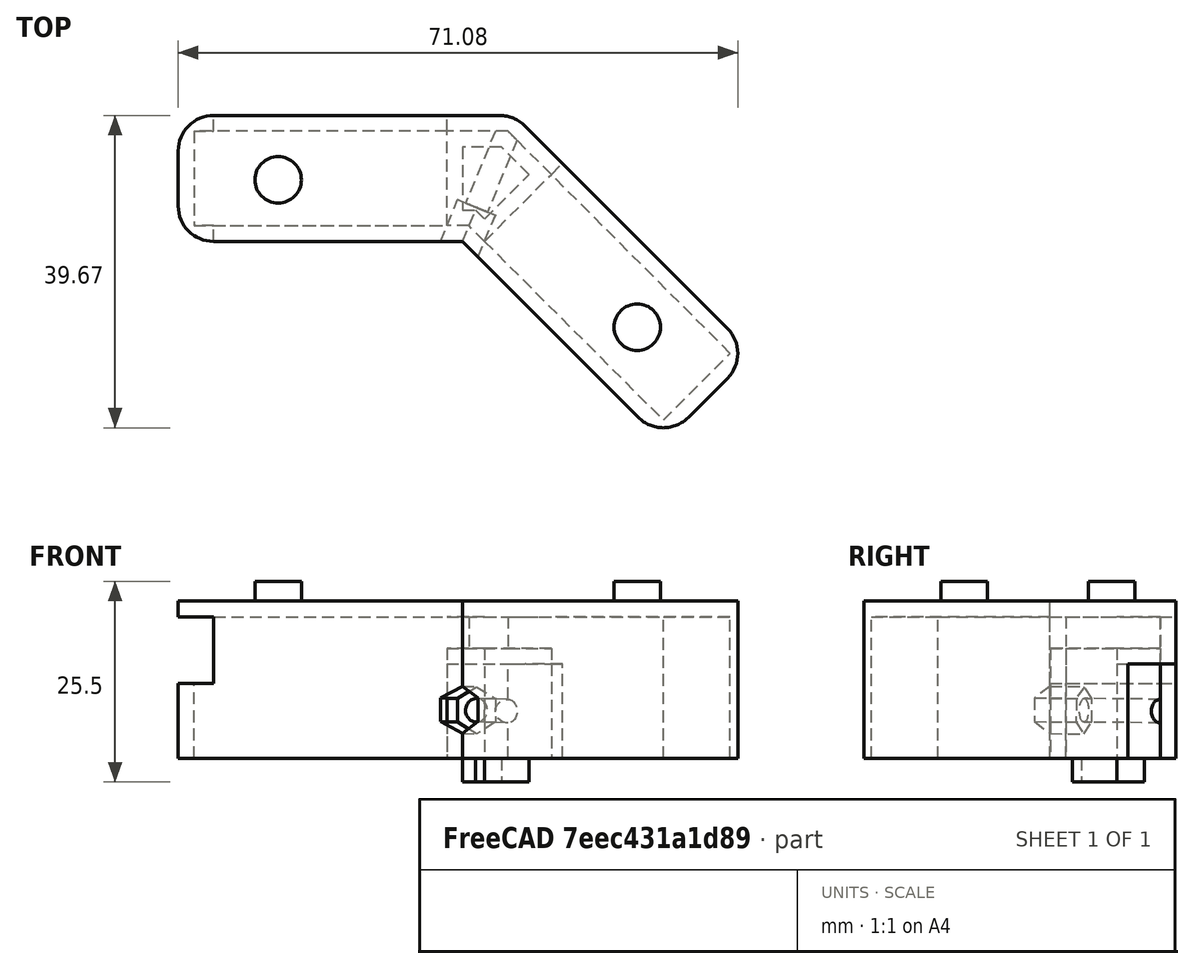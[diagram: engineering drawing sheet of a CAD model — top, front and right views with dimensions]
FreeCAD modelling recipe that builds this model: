
FCSTD DOCUMENT  (FreeCAD 0.19R)
Label: femur_btm
License: All rights reserved
LicenseURL: http://en.wikipedia.org/wiki/All_rights_reserved
objects: Sketcher::SketchObject×10, PartDesign::Pocket×6, PartDesign::Pad×4, PartDesign::Plane×1, PartDesign::Body×1
note: 32 computed .brp shape members not serialized (recipe doc carries the construction recipe); baked Part::Feature solids carry a one-line shape summary decoded from their .brp

FEATURE [Sketcher::SketchObject] Sketch004
  MapMode = 5
  Support = -> [XY_Plane001]
  sketch-geometry (21):
    g0: LineSegment [constr] StartX=-10.9452 StartY=6.06643 StartZ=0 EndX=20.9548 EndY=6.06643 EndZ=0
    g1: LineSegment [constr] StartX=20.9548 StartY=6.06643 StartZ=0 EndX=20.9548 EndY=-5.73357 EndZ=0
    g2: LineSegment [constr] StartX=20.9548 StartY=-5.73357 StartZ=0 EndX=-10.9452 EndY=-5.73357 EndZ=0
    g3: LineSegment [constr] StartX=-10.9452 StartY=-5.73357 StartZ=0 EndX=-10.9452 EndY=6.06643 EndZ=0
    g4: LineSegment StartX=-13.0452 StartY=-3.33357 StartZ=0 EndX=-13.0452 EndY=3.66643 EndZ=0
    g5: LineSegment StartX=-8.54522 StartY=8.16643 StartZ=0 EndX=27.8182 EndY=8.16643 EndZ=0
    g6: LineSegment StartX=31.0002 StartY=6.84841 StartZ=0 EndX=56.7131 EndY=-18.8644 EndZ=0
    g7: LineSegment StartX=56.7131 StartY=-25.2284 StartZ=0 EndX=51.7633 EndY=-30.1781 EndZ=0
    g8: LineSegment StartX=45.3994 StartY=-30.1781 StartZ=0 EndX=23.0548 EndY=-7.83357 EndZ=0
    g9: LineSegment StartX=23.0548 StartY=-7.83357 StartZ=0 EndX=-8.54522 EndY=-7.83357 EndZ=0
    g10: LineSegment [constr] StartX=-13.0452 StartY=3.66643 StartZ=0 EndX=-10.9452 EndY=3.66643 EndZ=0
    g11: LineSegment [constr] StartX=-8.54522 StartY=8.16643 StartZ=0 EndX=-8.54522 EndY=6.06643 EndZ=0
    g12: LineSegment [constr] StartX=-8.54522 StartY=-5.73357 StartZ=0 EndX=-8.54522 EndY=-7.83357 EndZ=0
    g13: LineSegment [constr] StartX=23.0548 StartY=-7.83357 StartZ=0 EndX=23.0548 EndY=8.16643 EndZ=0
    g14: LineSegment [constr] StartX=20.9548 StartY=-5.73357 StartZ=0 EndX=23.0548 EndY=-5.73357 EndZ=0
    g15: ArcOfCircle CenterX=-8.54522 CenterY=-3.33357 CenterZ=0 NormalX=0 NormalY=0 NormalZ=1 AngleXU=0 Radius=4.5 StartAngle=3.14159 EndAngle=4.71239
    g16: ArcOfCircle CenterX=-8.54522 CenterY=3.66643 CenterZ=0 NormalX=0 NormalY=0 NormalZ=1 AngleXU=0 Radius=4.5 StartAngle=1.5708 EndAngle=3.14159
    g17: ArcOfCircle CenterX=27.8182 CenterY=3.66643 CenterZ=0 NormalX=0 NormalY=0 NormalZ=1 AngleXU=0 Radius=4.5 StartAngle=0.785398 EndAngle=1.5708
    g18: ArcOfCircle CenterX=53.5311 CenterY=-22.0464 CenterZ=0 NormalX=0 NormalY=0 NormalZ=1 AngleXU=0 Radius=4.5 StartAngle=5.49779 EndAngle=7.06858
    g19: ArcOfCircle CenterX=48.5813 CenterY=-26.9962 CenterZ=0 NormalX=0 NormalY=0 NormalZ=1 AngleXU=0 Radius=4.5 StartAngle=3.92699 EndAngle=5.49779
    g20: LineSegment [constr] StartX=23.0548 StartY=-7.83357 StartZ=0 EndX=34.3685 EndY=3.48014 EndZ=0
  constraints (56):
    c: Coincident(g0,g1)
    c: Coincident(g1,g2)
    c: Coincident(g2,g3)
    c: Coincident(g3,g0)
    c: Horizontal(g0)
    c: Horizontal(g2)
    c: Vertical(g1)
    c: Vertical(g3)
    c: DistanceX(g0,g0) = 31.9
    c: DistanceY(g1,g1) = 11.8
    c: Vertical(g4)
    c: Horizontal(g5)
    c: Coincident(g8,g9)
    c: Horizontal(g9)
    c: Angle(g9,g8) = 2.35619
    c: Parallel(g8,g6)
    c: Perpendicular(g7,g8)
    c: Horizontal(g10)
    c: Vertical(g11)
    c: Vertical(g12)
    c: PointOnObject(g10,g3)
    c: PointOnObject(g11,g0)
    c: PointOnObject(g12,g2)
    c: Equal(g11,g10)
    c: Equal(g10,g12)
    c: DistanceY(g12,g12) = 2.1
    c: Coincident(g13,g8)
    c: PointOnObject(g13,g5)
    c: Vertical(g13)
    c: PointOnObject(g14,g13)
    c: Horizontal(g14)
    c: Equal(g14,g12)
    c: Tangent(g4,g15) = 1.5708
    c: Tangent(g9,g15) = 1.5708
    c: Tangent(g4,g16) = 1.5708
    c: Tangent(g5,g16) = 1.5708
    c: Tangent(g5,g17) = 1.5708
    c: Tangent(g6,g17) = 1.5708
    c: Tangent(g6,g18) = 1.5708
    c: Tangent(g7,g18) = 1.5708
    c: Tangent(g7,g19) = 1.5708
    c: Tangent(g8,g19) = 1.5708
    c: Equal(g19,g18)
    c: Equal(g18,g17)
    c: Equal(g17,g16)
    c: Equal(g16,g15)
    c: Radius(g18) = 4.5
    c: Equal(g8,g9)
    c: Coincident(g20,g8)
    c: PointOnObject(g20,g6)
    c: Perpendicular(g20,g8)
    c: Coincident(g10,g4)
    c: Coincident(g11,g5)
    c: Coincident(g12,g9)
    c: Coincident(g14,g1)
    c: Equal(g20,g13)
FEATURE [PartDesign::Pad] Pad003
  Length = 20
  Length2 = 100
  Profile = -> Sketch004
  Type = 0
FEATURE [Sketcher::SketchObject] Sketch005
  ExternalGeometry = -> [Pad003]
  MapMode = 5
  Placement = pos=(0,0,0) rot=(1,0,0;3.14159rad)
  Support = -> [Pad003]
  sketch-geometry (10):
    g0: LineSegment StartX=-11.0452 StartY=-6.16643 StartZ=0 EndX=-11.0452 EndY=5.83357 EndZ=0
    g1: LineSegment StartX=-11.0452 StartY=5.83357 StartZ=0 EndX=23.8832 EndY=5.83357 EndZ=0
    g2: LineSegment StartX=23.8832 StartY=5.83357 StartZ=0 EndX=48.5813 EndY=30.5317 EndZ=0
    g3: LineSegment StartX=48.5813 StartY=30.5317 StartZ=0 EndX=57.0666 EndY=22.0464 EndZ=0
    g4: LineSegment StartX=57.0666 StartY=22.0464 StartZ=0 EndX=28.8538 EndY=-6.16643 EndZ=0
    g5: LineSegment StartX=28.8538 StartY=-6.16643 StartZ=0 EndX=-11.0452 EndY=-6.16643 EndZ=0
    g6: LineSegment [constr] StartX=-13.0452 StartY=-3.66643 StartZ=0 EndX=-11.0452 EndY=-3.66643 EndZ=0
    g7: LineSegment [constr] StartX=-8.54522 StartY=7.83357 StartZ=0 EndX=-8.54522 EndY=5.83357 EndZ=0
    g8: LineSegment [constr] StartX=-8.54522 StartY=-8.16643 StartZ=0 EndX=-8.54522 EndY=-6.16643 EndZ=0
    g9: LineSegment [constr] StartX=51.7633 StartY=30.1781 StartZ=0 EndX=50.3491 EndY=28.7639 EndZ=0
  constraints (30):
    c: Vertical(g0)
    c: Coincident(g0,g1)
    c: Horizontal(g1)
    c: Coincident(g1,g2)
    c: Coincident(g2,g3)
    c: Coincident(g3,g4)
    c: Coincident(g4,g5)
    c: Coincident(g5,g0)
    c: Horizontal(g5)
    c: Coincident(g6,g-3)
    c: PointOnObject(g6,g0)
    c: Horizontal(g6)
    c: Coincident(g7,g-4)
    c: PointOnObject(g7,g1)
    c: Vertical(g7)
    c: Coincident(g8,g-5)
    c: PointOnObject(g8,g5)
    c: Vertical(g8)
    c: Equal(g8,g6)
    c: Equal(g6,g7)
    c: DistanceY(g8,g8) = 2
    c: Equal(g0,g3)
    c: Perpendicular(g3,g4)
    c: Parallel(g2,g4)
    c: Parallel(g4,g-6)
    c: Equal(g4,g5)
    c: Coincident(g9,g-7)
    c: PointOnObject(g9,g3)
    c: Perpendicular(g3,g9)
    c: Equal(g9,g8)
FEATURE [PartDesign::Pocket] Pocket001
  BaseFeature = -> Pad003
  Length = 18
  Length2 = 100
  Profile = -> Sketch005
  Type = 0
FEATURE [Sketcher::SketchObject] Sketch
  ExternalGeometry = -> [Pocket001]
  MapMode = 5
  Placement = pos=(0,-7.83357,0) rot=(1,0,0;1.5708rad)
  Support = -> [Pocket001]
  sketch-geometry (5):
    g0: GeomPoint X=-8.54522 Y=18 Z=0
    g1: LineSegment StartX=-8.54522 StartY=18 StartZ=0 EndX=-13.0452 EndY=18 EndZ=0
    g2: LineSegment StartX=-13.0452 StartY=18 StartZ=0 EndX=-13.0452 EndY=9.5 EndZ=0
    g3: LineSegment StartX=-13.0452 StartY=9.5 StartZ=0 EndX=-8.54522 EndY=9.5 EndZ=0
    g4: LineSegment StartX=-8.54522 StartY=9.5 StartZ=0 EndX=-8.54522 EndY=18 EndZ=0
  constraints (13):
    c: PointOnObject(g0,g-4)
    c: PointOnObject(g0,g-3)
    c: Coincident(g1,g2)
    c: Coincident(g2,g3)
    c: Coincident(g3,g4)
    c: Coincident(g4,g1)
    c: Horizontal(g1)
    c: Horizontal(g3)
    c: Vertical(g2)
    c: Vertical(g4)
    c: Coincident(g1,g0)
    c: PointOnObject(g2,g-5)
    c: DistanceY(g2,g2) = 8.5
FEATURE [PartDesign::Pocket] Pocket
  BaseFeature = -> Pocket001
  Length = 5
  Length2 = 100
  Profile = -> Sketch
  Type = 1
FEATURE [Sketcher::SketchObject] Sketch006
  ExternalGeometry = -> [Pocket]
  MapMode = 5
  Placement = pos=(0,0,18) rot=(1,0,0;3.14159rad)
  Support = -> [Pocket]
  sketch-geometry (6):
    g0: LineSegment StartX=21.0832 StartY=5.83357 StartZ=0 EndX=21.0832 EndY=-6.16643 EndZ=0
    g1: LineSegment StartX=25.8631 StartY=7.81346 StartZ=0 EndX=34.3484 EndY=-0.671817 EndZ=0
    g2: LineSegment StartX=21.0832 StartY=5.83357 StartZ=0 EndX=23.8832 EndY=5.83357 EndZ=0
    g3: LineSegment StartX=23.8832 StartY=5.83357 StartZ=0 EndX=25.8631 EndY=7.81346 EndZ=0
    g4: LineSegment StartX=34.3484 StartY=-0.671817 StartZ=0 EndX=28.8538 EndY=-6.16643 EndZ=0
    g5: LineSegment StartX=28.8538 StartY=-6.16643 StartZ=0 EndX=21.0832 EndY=-6.16643 EndZ=0
  constraints (16):
    c: Vertical(g0)
    c: Perpendicular(g1,g-5)
    c: PointOnObject(g1,g-5)
    c: PointOnObject(g0,g-6)
    c: PointOnObject(g0,g-3)
    c: PointOnObject(g1,g-4)
    c: Coincident(g0,g2)
    c: Coincident(g2,g-6)
    c: Coincident(g2,g3)
    c: Coincident(g3,g1)
    c: Coincident(g0,g5)
    c: Coincident(g5,g-4)
    c: Coincident(g4,g5)
    c: Coincident(g1,g4)
    c: Distance(g3) = 2.8
    c: Equal(g2,g3)
FEATURE [PartDesign::Pad] Pad
  BaseFeature = -> Pocket
  Length = 10
  Length2 = 100
  Profile = -> Sketch006
  Type = 3
  UpToFace = -> Pocket [Face4]
FEATURE [Sketcher::SketchObject] Sketch007
  ExternalGeometry = -> [Pad]
  MapMode = 5
  Placement = pos=(0,0,0) rot=(1,0,0;3.14159rad)
  Support = -> [Pad]
  sketch-geometry (7):
    g0: LineSegment [constr] StartX=23.8832 StartY=5.83357 StartZ=0 EndX=28.8538 EndY=-6.16643 EndZ=0
    g1: LineSegment StartX=23.0832 StartY=3.83357 StartZ=0 EndX=24.7116 EndY=3.83357 EndZ=0
    g2: LineSegment StartX=24.7116 StartY=3.83357 StartZ=0 EndX=25.8631 EndY=4.98504 EndZ=0
    g3: LineSegment StartX=25.8631 StartY=4.98504 StartZ=0 EndX=31.52 EndY=-0.671817 EndZ=0
    g4: LineSegment StartX=31.52 StartY=-0.671817 StartZ=0 EndX=28.0253 EndY=-4.16643 EndZ=0
    g5: LineSegment StartX=28.0253 StartY=-4.16643 StartZ=0 EndX=23.0832 EndY=-4.16643 EndZ=0
    g6: LineSegment StartX=23.0832 StartY=-4.16643 StartZ=0 EndX=23.0832 EndY=3.83357 EndZ=0
  constraints (20):
    c: Coincident(g0,g-3)
    c: Coincident(g0,g-4)
    c: PointOnObject(g1,g0)
    c: Coincident(g1,g2)
    c: Coincident(g2,g3)
    c: Coincident(g3,g4)
    c: PointOnObject(g4,g0)
    c: Coincident(g4,g5)
    c: Horizontal(g5)
    c: Coincident(g5,g6)
    c: Coincident(g6,g1)
    c: Vertical(g6)
    c: Horizontal(g1)
    c: Parallel(g-5,g2)
    c: Parallel(g2,g4)
    c: Equal(g1,g2)
    c: Equal(g5,g4)
    c: Distance(g1,g-3) = 2
    c: Distance(g3,g-4) = 2
    c: Distance(g5,g-6) = 2
FEATURE [PartDesign::Pad] Pad004
  BaseFeature = -> Pad
  Length = 3
  Length2 = 100
  Profile = -> Sketch007
  Type = 0
FEATURE [Sketcher::SketchObject] Sketch008
  ExternalGeometry = -> [Pad004]
  MapMode = 5
  Placement = pos=(0,0,0) rot=(1,0,0;3.14159rad)
  Support = -> [Pad004]
  sketch-geometry (7):
    g0: LineSegment StartX=21.0832 StartY=-6.16643 StartZ=0 EndX=21.0832 EndY=-8.16643 EndZ=0
    g1: LineSegment StartX=34.3484 StartY=-0.671817 StartZ=0 EndX=35.7626 EndY=-2.08603 EndZ=0
    g2: LineSegment StartX=21.0832 StartY=-8.16643 StartZ=0 EndX=27.8182 EndY=-8.16643 EndZ=0
    g3: LineSegment StartX=35.7626 StartY=-2.08603 StartZ=0 EndX=31.0002 EndY=-6.84841 EndZ=0
    g4: ArcOfCircle CenterX=27.8182 CenterY=-3.66643 CenterZ=0 NormalX=0 NormalY=0 NormalZ=1 AngleXU=0 Radius=4.5 StartAngle=4.71239 EndAngle=5.49779
    g5: LineSegment StartX=21.0832 StartY=-6.16643 StartZ=0 EndX=28.8538 EndY=-6.16643 EndZ=0
    g6: LineSegment StartX=28.8538 StartY=-6.16643 StartZ=0 EndX=34.3484 EndY=-0.671817 EndZ=0
  constraints (15):
    c: Coincident(g0,g-3)
    c: PointOnObject(g0,g-6)
    c: Vertical(g0)
    c: Coincident(g1,g-4)
    c: Perpendicular(g1,g-5)
    c: Coincident(g2,g0)
    c: Coincident(g3,g1)
    c: Tangent(g2,g4) = -1.5708
    c: Tangent(g3,g4) = 1.5708
    c: Coincident(g3,g-5)
    c: Coincident(g2,g-6)
    c: Coincident(g0,g5)
    c: Coincident(g5,g-7)
    c: Coincident(g5,g6)
    c: Coincident(g6,g1)
FEATURE [PartDesign::Pocket] Pocket002
  BaseFeature = -> Pad004
  Length = 12
  Length2 = 100
  Profile = -> Sketch008
  Type = 0
FEATURE [PartDesign::Plane] DatumPlane
  AttachmentOffset = pos=(-6,0,0) rot=(0,1,0;1.5708rad)
  Length = 64.9992
  MapMode = 45
  Placement = pos=(20.9961,-12.8037,1.05295) rot=(-0.48682,0.728578,0.481851;1.89204rad)
  ResizeMode = 0
  Support = -> [Sketch004,Pocket002]
  Width = 112.435
FEATURE [Sketcher::SketchObject] Sketch009
  ExternalGeometry = -> [Pocket002]
  MapMode = 5
  Placement = pos=(20.9961,-12.8037,1.05295) rot=(-0.48682,0.728578,0.481851;1.89204rad)
  Support = -> [DatumPlane]
  sketch-geometry (3):
    g0: Circle CenterX=-5.15743 CenterY=-4.5919e-12 CenterZ=0 NormalX=0 NormalY=0 NormalZ=1 AngleXU=0 Radius=1.5
    g1: LineSegment [constr] StartX=-11.1571 StartY=-4.4906e-12 StartZ=0 EndX=-5.15743 EndY=-4.5919e-12 EndZ=0
    g2: LineSegment [constr] StartX=-5.15743 StartY=-4.5919e-12 StartZ=0 EndX=0.842251 EndY=-4.6931e-12 EndZ=0
  constraints (7):
    c: Radius(g0) = 1.5
    c: Coincident(g1,g2)
    c: Coincident(g2,g-3)
    c: Coincident(g1,g-3)
    c: PointOnObject(g1,g-3)
    c: Equal(g1,g2)
    c: Coincident(g0,g1)
FEATURE [PartDesign::Pocket] Pocket003
  BaseFeature = -> Pocket002
  Length = 5
  Length2 = 100
  Profile = -> Sketch009
  Reversed = true
  Type = 1
FEATURE [Sketcher::SketchObject] Sketch010
  ExternalGeometry = -> [Pocket003,Pocket002]
  MapMode = 5
  Placement = pos=(20.9961,-12.8037,1.05295) rot=(-0.48682,0.728578,0.481851;1.89204rad)
  Support = -> [DatumPlane]
  sketch-geometry (9):
    g0: LineSegment [constr] StartX=-11.1571 StartY=-4.4906e-12 StartZ=0 EndX=-5.15743 EndY=-4.5919e-12 EndZ=0
    g1: LineSegment [constr] StartX=-5.15743 StartY=-4.5919e-12 StartZ=0 EndX=0.842251 EndY=-4.6931e-12 EndZ=0
    g2: LineSegment StartX=-3.65743 StartY=-2.59808 StartZ=0 EndX=-2.15743 EndY=-4.6425e-12 EndZ=0
    g3: LineSegment StartX=-2.15743 StartY=-4.6425e-12 StartZ=0 EndX=-3.65743 EndY=2.59808 EndZ=0
    g4: LineSegment StartX=-3.65743 StartY=2.59808 StartZ=0 EndX=-6.65743 EndY=2.59808 EndZ=0
    g5: LineSegment StartX=-6.65743 StartY=2.59808 StartZ=0 EndX=-8.15743 EndY=-4.5408e-12 EndZ=0
    g6: LineSegment StartX=-8.15743 StartY=-4.541e-12 StartZ=0 EndX=-6.65743 EndY=-2.59808 EndZ=0
    g7: LineSegment StartX=-6.65743 StartY=-2.59808 StartZ=0 EndX=-3.65743 EndY=-2.59808 EndZ=0
    g8: Circle [constr] CenterX=-5.15743 CenterY=-4.5919e-12 CenterZ=0 NormalX=0 NormalY=0 NormalZ=1 AngleXU=0 Radius=3
  constraints (21):
    c: Coincident(g0,g1)
    c: Coincident(g1,g-4)
    c: Coincident(g0,g-4)
    c: PointOnObject(g0,g-4)
    c: Equal(g0,g1)
    c: Coincident(g2,g3)
    c: Coincident(g3,g4)
    c: Coincident(g4,g5)
    c: Coincident(g5,g6)
    c: Coincident(g6,g7)
    c: Coincident(g7,g2)
    c: Equal(g2, g3-g7) x5
    c: PointOnObject(g2,g8)
    c: PointOnObject(g3,g8)
    c: PointOnObject(g4,g8)
    c: PointOnObject(g5,g8)
    c: PointOnObject(g6,g8)
    c: PointOnObject(g7,g8)
    c: Coincident(g8,g0)
    c: PointOnObject(g2,g0)
    c: Radius(g8) = 3
FEATURE [PartDesign::Pocket] Pocket004
  BaseFeature = -> Pocket003
  Length = 10
  Length2 = 100
  Profile = -> Sketch010
  Reversed = true
  Type = 0
FEATURE [Sketcher::SketchObject] Sketch011
  ExternalGeometry = -> [Pocket004]
  MapMode = 5
  Placement = pos=(0,0,18) rot=(1,0,0;3.14159rad)
  Support = -> [Pocket004]
  sketch-geometry (6):
    g0: LineSegment StartX=21.0832 StartY=5.83357 StartZ=0 EndX=21.0832 EndY=-6.16643 EndZ=0
    g1: LineSegment StartX=21.0832 StartY=-6.16643 StartZ=0 EndX=28.8538 EndY=-6.16643 EndZ=0
    g2: LineSegment StartX=28.8538 StartY=-6.16643 StartZ=0 EndX=34.3484 EndY=-0.671817 EndZ=0
    g3: LineSegment StartX=34.3484 StartY=-0.671817 StartZ=0 EndX=25.8631 EndY=7.81346 EndZ=0
    g4: LineSegment StartX=25.8631 StartY=7.81346 StartZ=0 EndX=23.8832 EndY=5.83357 EndZ=0
    g5: LineSegment StartX=23.8832 StartY=5.83357 StartZ=0 EndX=21.0832 EndY=5.83357 EndZ=0
  constraints (12):
    c: Coincident(g-5,g0)
    c: Coincident(g0,g-7)
    c: Coincident(g0,g1)
    c: Coincident(g1,g-8)
    c: Coincident(g1,g2)
    c: Coincident(g2,g-8)
    c: Coincident(g2,g3)
    c: Coincident(g3,g-6)
    c: Coincident(g3,g4)
    c: Coincident(g4,g-6)
    c: Coincident(g4,g5)
    c: Coincident(g5,g0)
FEATURE [PartDesign::Pocket] Pocket005
  BaseFeature = -> Pocket004
  Length = 4
  Length2 = 100
  Profile = -> Sketch011
  Reversed = true
  Type = 0
FEATURE [Sketcher::SketchObject] Sketch012
  ExternalGeometry = -> [Pocket005]
  MapMode = 5
  Placement = pos=(0,0,20) rot=(0,0,1;0rad)
  Support = -> [Pocket005]
  sketch-geometry (5):
    g0: LineSegment [constr] StartX=-13.0452 StartY=0 StartZ=0 EndX=-0.345215 EndY=0 EndZ=0
    g1: Circle CenterX=-0.345215 CenterY=0 CenterZ=0 NormalX=0 NormalY=0 NormalZ=1 AngleXU=0 Radius=2.95
    g2: LineSegment [constr] StartX=45.2579 StartY=-18.723 StartZ=0 EndX=54.2382 EndY=-27.7033 EndZ=0
    g3: LineSegment [constr] StartX=54.2382 StartY=-27.7033 StartZ=0 EndX=56.7131 EndY=-25.2284 EndZ=0
    g4: Circle CenterX=45.2579 CenterY=-18.723 CenterZ=0 NormalX=0 NormalY=0 NormalZ=1 AngleXU=0 Radius=2.95
  constraints (15):
    c: Horizontal(g0)
    c: DistanceX(g0,g0) = 12.7
    c: PointOnObject(g0,g-3)
    c: PointOnObject(g0,g-1)
    c: Coincident(g1,g0)
    c: Radius(g1) = 2.95
    c: Distance(g-4) = 7
    c: Coincident(g3,g2)
    c: Perpendicular(g3,g2)
    c: Parallel(g2,g-5)
    c: Distance(g3) = 3.5
    c: Coincident(g3,g-4)
    c: Equal(g2,g0)
    c: Coincident(g4,g2)
    c: Equal(g4,g1)
FEATURE [PartDesign::Pad] Pad005
  BaseFeature = -> Pocket005
  Length = 2.5
  Length2 = 100
  Profile = -> Sketch012
  Type = 0
FEATURE [PartDesign::Body] Body001  label="tibia_btm"
  Group = -> [Sketch004,Pad003,Sketch005,Pocket001,Sketch,Pocket,Sketch006,Pad,Sketch007,Pad004,Sketch008,Pocket002,DatumPlane,Sketch009,Pocket003,Sketch010,Pocket004,Sketch011,Pocket005,Sketch012,Pad005]
  Origin = -> Origin001
  Tip = -> Pad005
